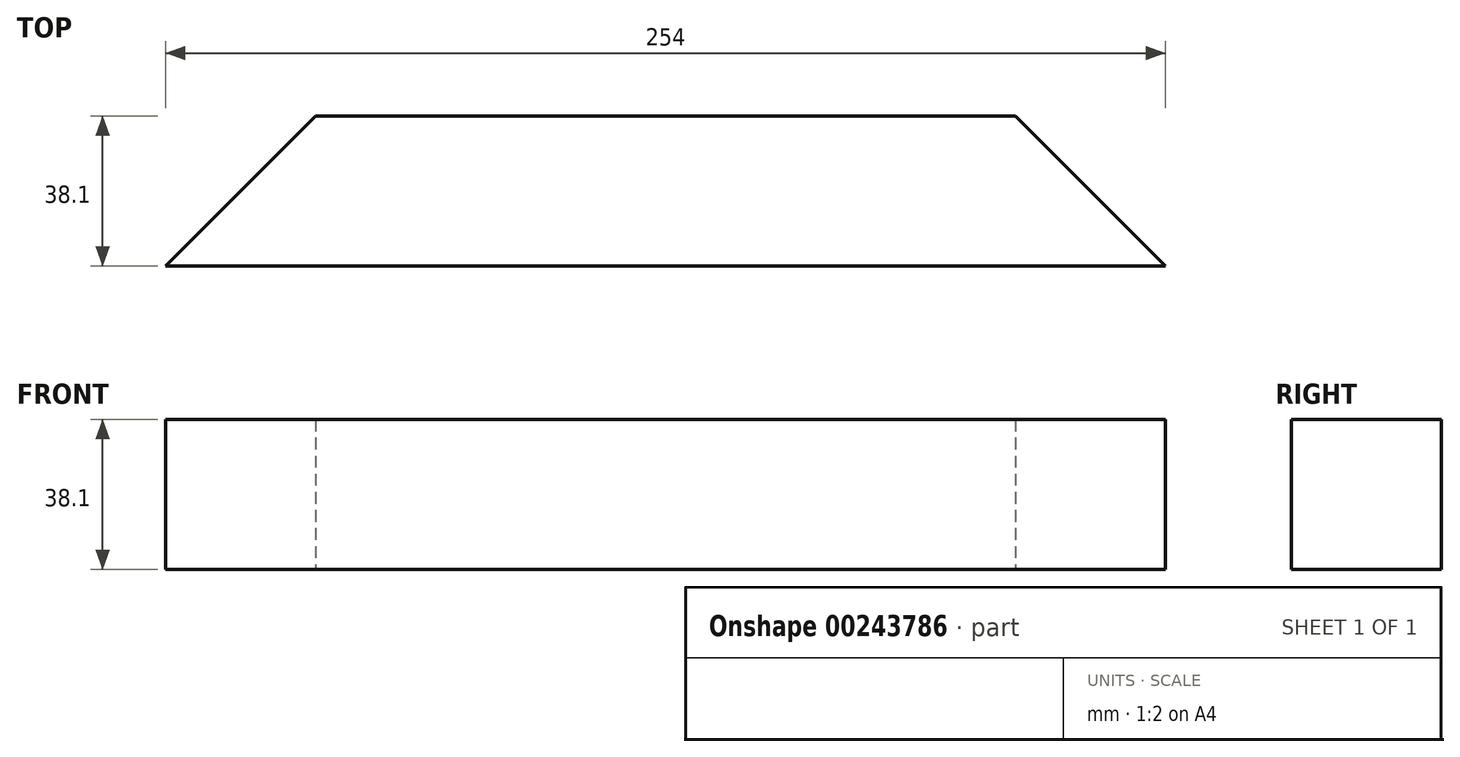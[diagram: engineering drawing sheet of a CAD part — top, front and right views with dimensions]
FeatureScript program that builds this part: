
annotation { "Feature Type Name" : "Feature", "Feature Type Description" : "" }
export const myFeature = defineFeature(function(context is Context, id is Id, definition is map)
    precondition{}
    {
        {
            var Q0;
            Q0=qCreatedBy(makeId("Top.planeOp"),FACE);
            var sketch = newSketch(context, id + "F0", { "sketchPlane" : qUnion([Q0])});
            skLineSegment(sketch, "E0.bottom", {"start": v(-55.88, 38.1) * mm, "end": v(121.92, 38.1) * mm});
            skLineSegment(sketch, "E0.top", {"start": v(-93.98, 0) * mm, "end": v(160.02, 0) * mm});
            skLineSegment(sketch, "E1", {"start": v(-55.88, 38.1) * mm, "end": v(-93.98, 0) * mm});
            skLineSegment(sketch, "E2", {"start": v(121.92, 38.1) * mm, "end": v(160.02, 0) * mm});
            skSolve(sketch);
        }
        {
            var Q0;
            Q0=makeQuery(id+"F0.imprint","IMPRINT",FACE,{"disambiguationData":[TD([[makeQuery(id+"F0.imprint","IMPRINT",EDGE,{"derivedFrom":sQuery(id+"F0.wireOp",EDGE,"E0.bottom")}),-1.0]])]});
            extrude(context, id + "F1", {"entities" : qUnion([Q0]), "depth" : 38.1 * mm});
        }
    });
